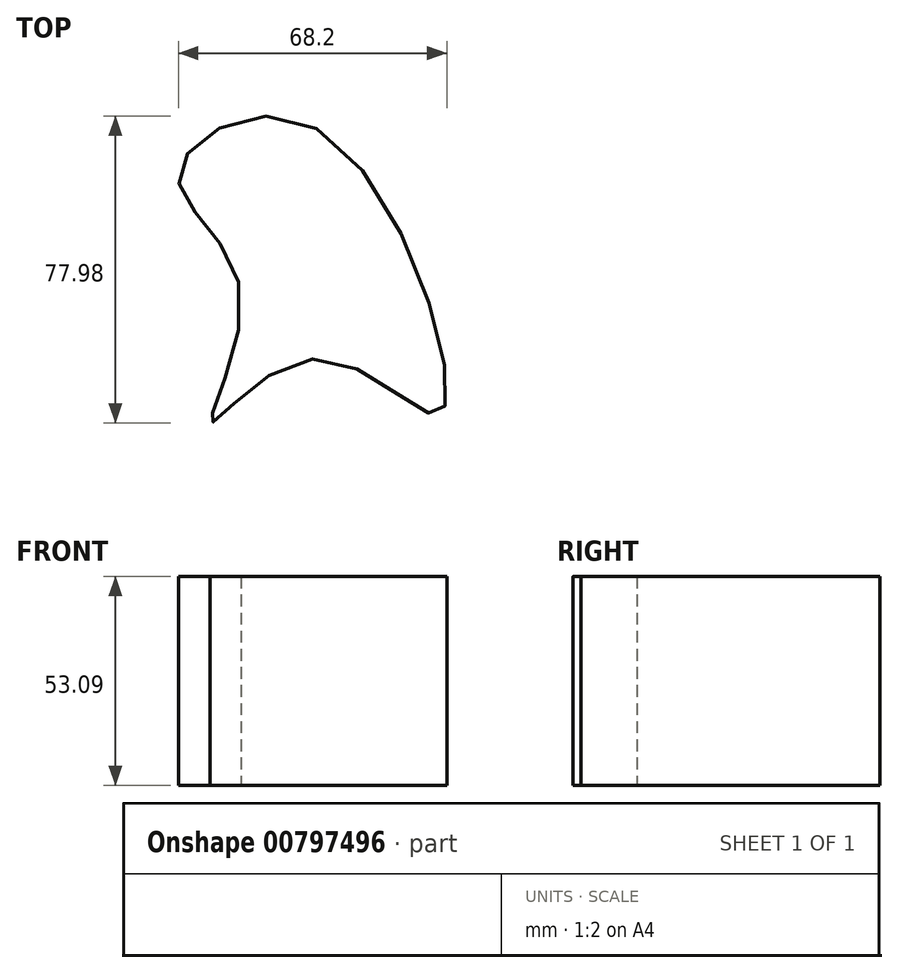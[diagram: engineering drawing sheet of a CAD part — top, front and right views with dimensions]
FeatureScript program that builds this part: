
annotation { "Feature Type Name" : "Feature", "Feature Type Description" : "" }
export const myFeature = defineFeature(function(context is Context, id is Id, definition is map)
    precondition{}
    {
        {
            var Q0;
            Q0=qCreatedBy(makeId("Top.planeOp"),FACE);
            var sketch = newSketch(context, id + "F0", { "sketchPlane" : qUnion([Q0])});
            skFitSpline(sketch, "E0", {"points": [v(0, 40.57) * mm, v(-35.01, 29.09) * mm, v(-19.45, 0) * mm, v(-26.86, -34.27) * mm, v(0, -17.97) * mm, v(31.68, -31.68) * mm, v(0, 40.57) * mm]});
            skSolve(sketch);
        }
        {
            var Q0;
            Q0=makeQuery(id+"F0.imprint","IMPRINT",FACE,{"disambiguationData":[TD([[makeQuery(id+"F0.imprint","IMPRINT",EDGE,{"derivedFrom":sQuery(id+"F0.wireOp",EDGE,"E0")}),1.0]])]});
            extrude(context, id + "F1", {"entities" : qUnion([Q0]), "depth" : 53.1 * mm, "offsetDistance" : 25.4 * mm});
        }
    });
